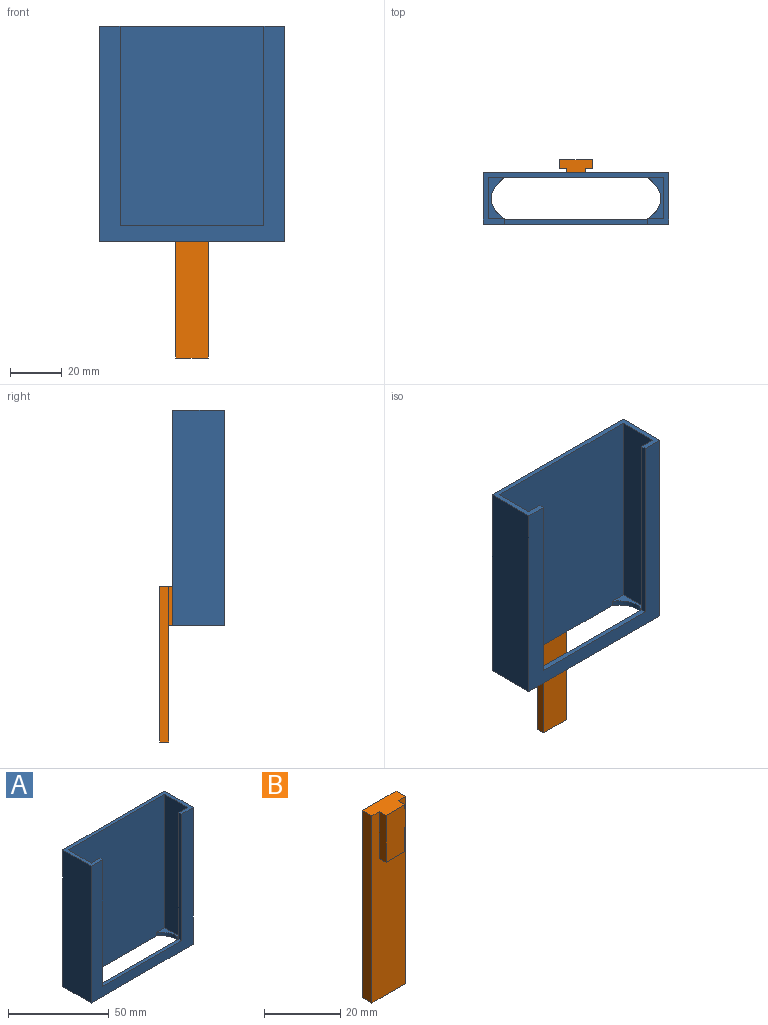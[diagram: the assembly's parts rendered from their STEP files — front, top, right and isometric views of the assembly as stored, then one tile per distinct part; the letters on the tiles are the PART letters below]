
ASSEMBLY  parts=2 mates=1
PART A: 21 faces, bbox 71.5x20x83 mm
  f0: plane 83x71.5mm, normal (0,1,0), area 5829.5mm2, adj f1,f6,f7,f8,f17,f18,f19
  f1: plane 71.5x20mm, normal (0,0,1), area 239mm2, adj f0,f2,f3,f7,f8,f9,f11,f13
  f2: plane 83x71.5mm, normal (0,-1,0), area 1661mm2, adj f1,f6,f7,f8,f14,f15,f16
  f3: plane 83x67.5mm, normal (0,1,0), area 1305mm2, adj f1,f4,f5,f6,f10,f11,f12,f13
  f4: extruded ~16x5mm, area 39mm2, adj f3,f6,f9,f12
  f5: extruded ~16x5mm, area 39mm2, adj f3,f6,f9,f10
  f6: plane 71.5x20mm, normal (0,0,-1), area 428.3mm2, adj f0,f2,f3,f4,f5,f7,f8,f9
  f7: plane 83x20mm, normal (-1,0,0), area 1660mm2, adj f0,f1,f2,f6
  f8: plane 83x20mm, normal (1,0,0), area 1660mm2, adj f0,f1,f2,f6
  f9: plane 83x67.5mm, normal (0,-1,0), area 5578.5mm2, adj f1,f4,f5,f6,f10,f11,f12,f13
  f10: plane 16x6.88mm, normal (0,0,1), area 42.7mm2, adj f3,f5,f9,f11
  f11: plane 81x16mm, normal (-1,0,0), area 1296mm2, adj f1,f3,f9,f10
  f12: plane 16x6.88mm, normal (0,0,1), area 42.7mm2, adj f3,f4,f9,f13
  f13: plane 81x16mm, normal (1,0,0), area 1296mm2, adj f1,f3,f9,f12
  f14: plane 77x2mm, normal (1,0,0), area 154mm2, adj f1,f2,f3,f15
  f15: plane 55.5x2mm, normal (0,0,1), area 111mm2, adj f2,f3,f14,f16
  f16: plane 77x2mm, normal (-1,0,0), area 154mm2, adj f1,f2,f3,f15
  f17: plane 15x1mm, normal (-1,0,0), area 15mm2, adj f0,f6,f19,f20
  f18: plane 15x1mm, normal (1,0,0), area 15mm2, adj f0,f6,f19,f20
  f19: plane 7x1mm, normal (0,0,-1), area 7mm2, adj f0,f17,f18,f20
  f20: plane 15x7mm, normal (0,1,0), area 105mm2, adj f6,f17,f18,f19
PART B: 10 faces, bbox 12.5x6x60 mm
  f0: plane 15x7mm, normal (0,-1,0), area 105mm2, adj f1,f2,f8,f9
  f1: plane 15x2.5mm, normal (1,0,0), area 37.5mm2, adj f0,f7,f8,f9
  f2: plane 15x2.5mm, normal (-1,0,0), area 37.5mm2, adj f0,f7,f8,f9
  f3: plane 12.5x3.5mm, normal (0,0,-1), area 43.8mm2, adj f4,f5,f6,f7
  f4: plane 60x3.5mm, normal (1,0,0), area 210mm2, adj f3,f5,f7,f8
  f5: plane 60x12.5mm, normal (0,1,0), area 750mm2, adj f3,f4,f6,f8
  f6: plane 60x3.5mm, normal (-1,0,0), area 210mm2, adj f3,f5,f7,f8
  f7: plane 60x12.5mm, normal (0,-1,0), area 645mm2, adj f1,f2,f3,f4,f6,f8,f9
  f8: plane 12.5x6mm, normal (0,0,1), area 61.3mm2, adj f0,f1,f2,f4,f5,f6,f7
  f9: plane 7x2.5mm, normal (0,0,-1), area 17.5mm2, adj f0,f1,f2,f7
PLACE A t=(0,46.9,-8.5)mm
PLACE B t=(0,55.9,-53.5)mm
MATE fastened A.f20 <-> B.f0  axis (0,1,0) through (0,55.9,-1)mm
